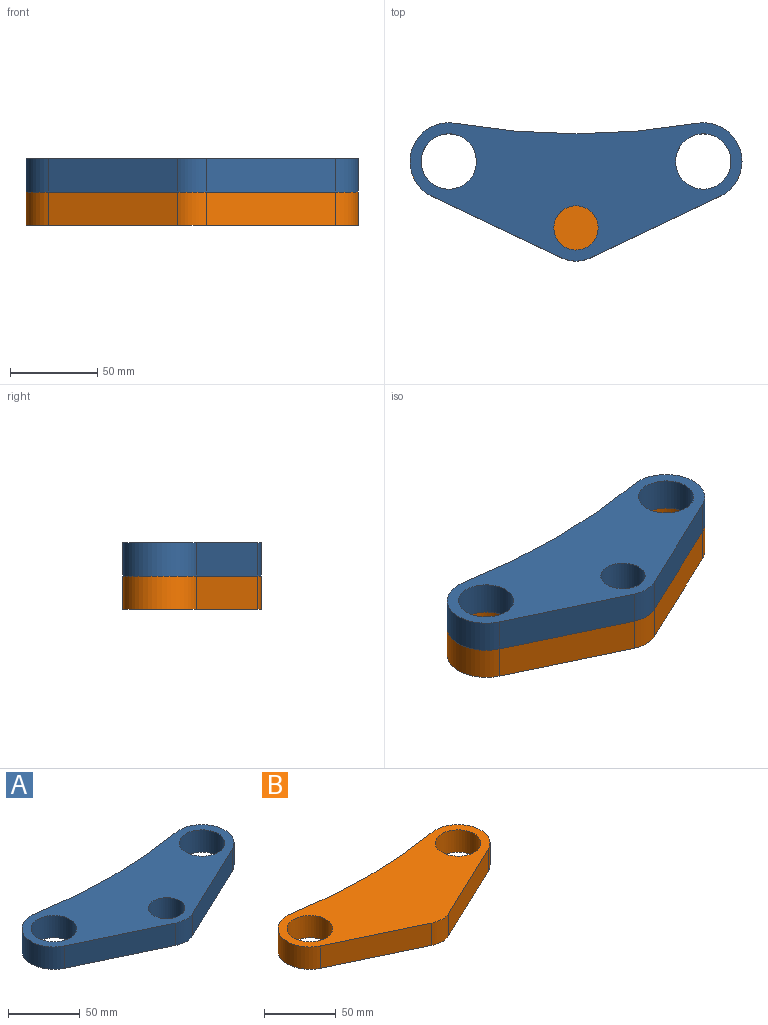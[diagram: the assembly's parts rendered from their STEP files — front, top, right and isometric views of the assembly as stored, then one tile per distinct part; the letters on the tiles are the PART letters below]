
ASSEMBLY  parts=2 mates=1
PART A: 11 faces, bbox 190.5x79.4x19.1 mm
  f0: plane 74.38x35.23mm, normal (-0.43,-0.9,0), area 1567.9mm2, adj f1,f8,f9,f10
  f1: cylinder r=19.05mm len=19.05mm, axis (0,0,-1), area 321mm2, adj f0,f2,f9,f10
  f2: plane 74.38x35.23mm, normal (0.43,-0.9,0), area 1567.9mm2, adj f1,f3,f9,f10
  f3: cylinder r=22.23mm len=42.31mm, axis (0,0,-1), area 1216.3mm2, adj f2,f4,f9,f10
  f4: cylinder r=400.84mm len=138.38mm, axis (0,0,-1), area 2649.4mm2, adj f3,f8,f9,f10
  f5: cylinder r=15.88mm len=31.75mm, axis (0,0,-1), area 1900.2mm2, adj f9,f10
  f6: cylinder r=15.88mm len=31.75mm, axis (0,0,-1), area 1900.2mm2, adj f9,f10
  f7: cylinder r=12.7mm len=25.4mm, axis (0,0,-1), area 1520.1mm2, adj f9,f10
  f8: cylinder r=22.23mm len=42.31mm, axis (0,0,-1), area 1216.3mm2, adj f0,f4,f9,f10
  f9: plane 190.5x79.38mm, normal (0,0,1), area 8226.2mm2, adj f0,f1,f2,f3,f4,f5,f6,f7
  f10: plane 190.5x79.38mm, normal (0,0,-1), area 8226.2mm2, adj f0,f1,f2,f3,f4,f5,f6,f7
PART B: 10 faces, bbox 190.5x79.4x19.1 mm
  f0: plane 74.38x35.23mm, normal (-0.43,-0.9,0), area 1567.9mm2, adj f1,f7,f8,f9
  f1: cylinder r=19.05mm len=19.05mm, axis (0,0,-1), area 321mm2, adj f0,f2,f8,f9
  f2: plane 74.38x35.23mm, normal (0.43,-0.9,0), area 1567.9mm2, adj f1,f3,f8,f9
  f3: cylinder r=22.23mm len=42.31mm, axis (0,0,-1), area 1216.3mm2, adj f2,f4,f8,f9
  f4: cylinder r=400.84mm len=138.38mm, axis (0,0,-1), area 2649.4mm2, adj f3,f7,f8,f9
  f5: cylinder r=15.88mm len=31.75mm, axis (0,0,-1), area 1900.2mm2, adj f8,f9
  f6: cylinder r=15.88mm len=31.75mm, axis (0,0,-1), area 1900.2mm2, adj f8,f9
  f7: cylinder r=22.23mm len=42.31mm, axis (0,0,-1), area 1216.3mm2, adj f0,f4,f8,f9
  f8: plane 190.5x79.38mm, normal (0,0,1), area 8732.9mm2, adj f0,f1,f2,f3,f4,f5,f6,f7
  f9: plane 190.5x79.38mm, normal (0,0,-1), area 8732.9mm2, adj f0,f1,f2,f3,f4,f5,f6,f7
PLACE A t=(278.45,0,19.05)mm
PLACE B t=(278.45,0,0)mm
MATE fastened A.f1 <-> B.f1  axis (0,0,-1) through (351.47,-38.1,19.05)mm
